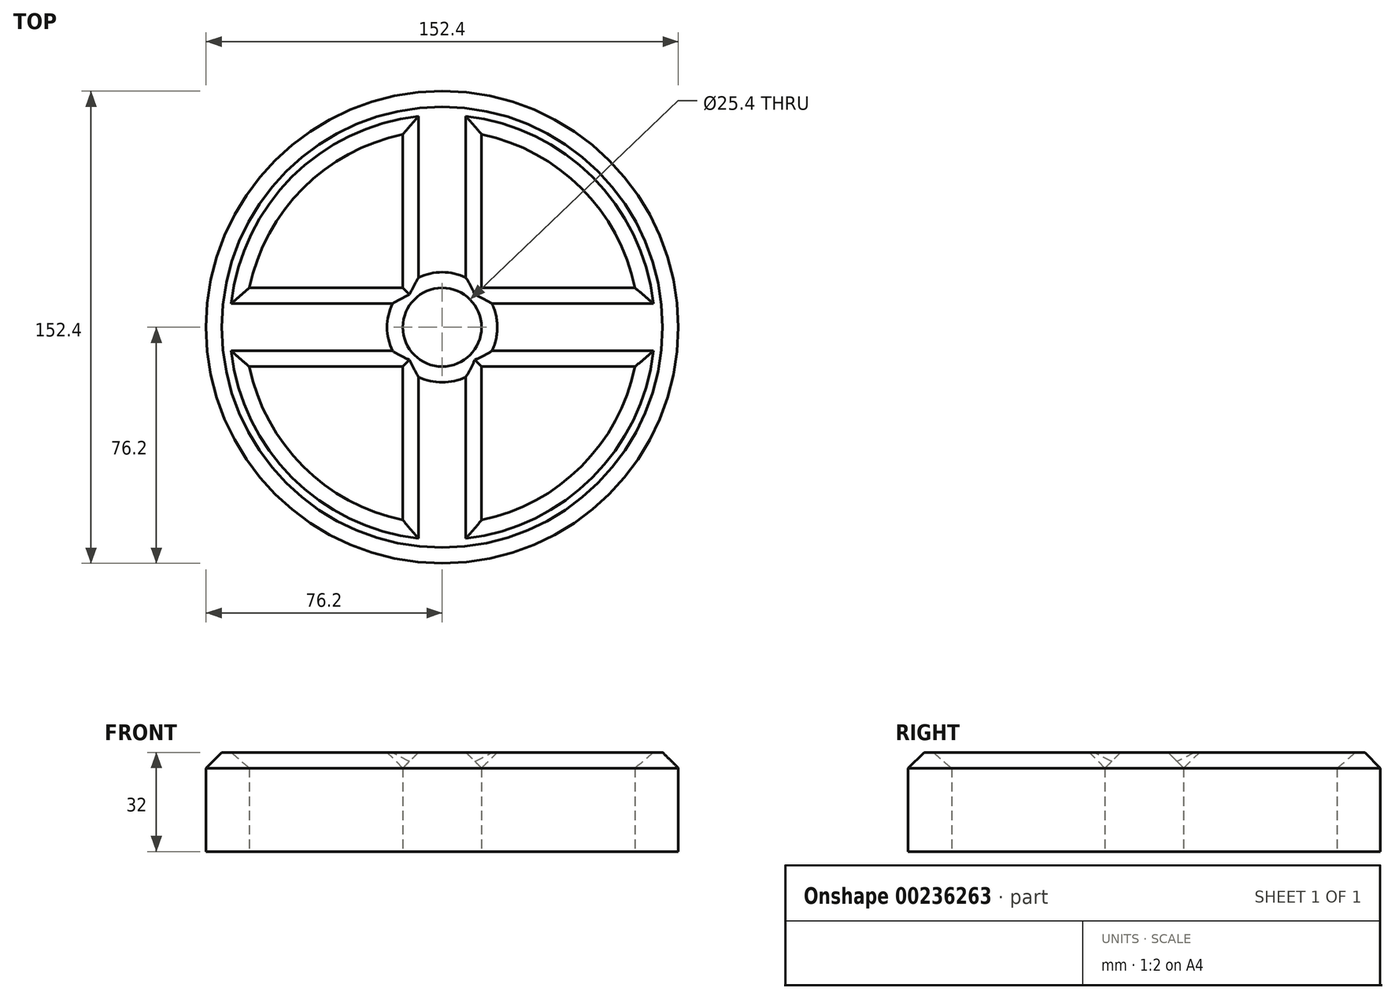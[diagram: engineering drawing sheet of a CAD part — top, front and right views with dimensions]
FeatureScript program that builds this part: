
annotation { "Feature Type Name" : "Feature", "Feature Type Description" : "" }
export const myFeature = defineFeature(function(context is Context, id is Id, definition is map)
    precondition{}
    {
        {
            var Q0;
            Q0=qCreatedBy(makeId("Top.planeOp"),FACE);
            var sketch = newSketch(context, id + "F0", { "sketchPlane" : qUnion([Q0])});
            skCircle(sketch, "E0", {"center": v(0, 0) * mm, "radius": 76.2 * mm});
            skCircle(sketch, "E1", {"center": v(0, 0) * mm, "radius": 12.7 * mm});
            skPoint(sketch, "E2.center.orphan", {"position": v(0, -1.65) * mm});
            skArc(sketch, "E3", {"start": v(-62.22, -12.7) * mm, "mid": v(-44.9, -44.9) * mm, "end": v(-12.7, -62.22) * mm});
            skLineSegment(sketch, "E4", {"start": v(0, 0) * mm, "end": v(0, 63.5) * mm});
            skLineSegment(sketch, "E5.0", {"start": v(12.7, 12.7) * mm, "end": v(12.7, 62.22) * mm});
            skLineSegment(sketch, "E6.0", {"start": v(-12.7, 12.7) * mm, "end": v(-12.7, 62.22) * mm});
            skLineSegment(sketch, "E7", {"start": v(0, -1.65) * mm, "end": v(0, -63.5) * mm});
            skLineSegment(sketch, "E8", {"start": v(0, 0) * mm, "end": v(63.5, 0) * mm});
            skLineSegment(sketch, "E9", {"start": v(0, 0) * mm, "end": v(-76.2, 0) * mm});
            skLineSegment(sketch, "E10.0", {"start": v(-12.7, -12.7) * mm, "end": v(-12.7, -62.22) * mm});
            skLineSegment(sketch, "E11.0", {"start": v(12.7, -12.7) * mm, "end": v(12.7, -62.22) * mm});
            skLineSegment(sketch, "E12.0", {"start": v(12.7, -12.7) * mm, "end": v(62.22, -12.7) * mm});
            skLineSegment(sketch, "E13", {"start": v(-76.2, 0) * mm, "end": v(0, 0) * mm});
            skLineSegment(sketch, "E14.0", {"start": v(-12.7, 12.7) * mm, "end": v(-62.22, 12.7) * mm});
            skLineSegment(sketch, "E15.0", {"start": v(-12.7, -12.7) * mm, "end": v(-62.22, -12.7) * mm});
            skLineSegment(sketch, "E16.0", {"start": v(12.7, 12.7) * mm, "end": v(62.22, 12.7) * mm});
            skLineSegment(sketch, "E17.trimOffspring", {"start": v(-12.7, 75.13) * mm, "end": v(-12.7, 76.2) * mm});
            skLineSegment(sketch, "E18.trimOffspring", {"start": v(12.7, 75.13) * mm, "end": v(12.7, 76.2) * mm});
            skLineSegment(sketch, "E19.trimOffspring", {"start": v(12.7, -75.13) * mm, "end": v(12.7, -76.2) * mm});
            skLineSegment(sketch, "E20.trimOffspring", {"start": v(-12.7, -75.13) * mm, "end": v(-12.7, -76.2) * mm});
            skLineSegment(sketch, "E21.trimOffspring", {"start": v(-75.13, 12.7) * mm, "end": v(-76.2, 12.7) * mm});
            skLineSegment(sketch, "E22.trimOffspring", {"start": v(-75.13, -12.7) * mm, "end": v(-76.2, -12.7) * mm});
            skLineSegment(sketch, "E23.trimOffspring", {"start": v(75.13, -12.7) * mm, "end": v(76.2, -12.7) * mm});
            skLineSegment(sketch, "E24.trimOffspring", {"start": v(75.13, 12.7) * mm, "end": v(76.2, 12.7) * mm});
            skArc(sketch, "E25.trimOffspring", {"start": v(-12.7, 62.22) * mm, "mid": v(-44.9, 44.9) * mm, "end": v(-62.22, 12.7) * mm});
            skArc(sketch, "E26.trimOffspring", {"start": v(62.22, 12.7) * mm, "mid": v(44.9, 44.9) * mm, "end": v(12.7, 62.22) * mm});
            skArc(sketch, "E27.trimOffspring", {"start": v(12.7, -62.22) * mm, "mid": v(44.9, -44.9) * mm, "end": v(62.22, -12.7) * mm});
            skLineSegment(sketch, "E28.bottom", {"start": v(-8.56, -9.38) * mm, "end": v(8.56, -9.38) * mm});
            skLineSegment(sketch, "E28.top", {"start": v(-8.56, 9.38) * mm, "end": v(8.56, 9.38) * mm});
            skLineSegment(sketch, "E28.left", {"start": v(-8.56, -9.38) * mm, "end": v(-8.56, 9.38) * mm});
            skLineSegment(sketch, "E28.right", {"start": v(8.56, -9.38) * mm, "end": v(8.56, 9.38) * mm});
            skLineSegment(sketch, "E29", {"start": v(0, 0) * mm, "end": v(44.9, 44.9) * mm});
            skLineSegment(sketch, "E30", {"start": v(0, 0) * mm, "end": v(-9.18, 8.77) * mm});
            skLineSegment(sketch, "E31", {"start": v(0, 0) * mm, "end": v(44.9, -44.9) * mm});
            skSolve(sketch);
        }
        {
            var Q0;
            Q0 = qSketchRegion(id + "F0", true);
            extrude(context, id + "F1", {"entities" : qUnion([Q0]), "depth" : 32 * mm});
        }
        {
            var Q0;
            Q0 = qSketchRegion(id + "F0", true);
            extrude(context, id + "F2", {"entities" : qUnion([Q0]), "operationType" : NewBodyOperationType.ADD, "depth" : 25.4 * mm});
        }
        {
            var Q0;
            Q0=makeQuery(id+"F1.opExtrude","CAP_FACE",FACE,{"disambiguationData":[OSD([sQuery(id+"F0.wireOp",EDGE,"E0"),sQuery(id+"F0.wireOp",EDGE,"E1"),sQuery(id+"F0.wireOp",EDGE,"E3"),sQuery(id+"F0.wireOp",EDGE,"E5.0"),sQuery(id+"F0.wireOp",EDGE,"E6.0"),sQuery(id+"F0.wireOp",EDGE,"E10.0"),sQuery(id+"F0.wireOp",EDGE,"E11.0"),sQuery(id+"F0.wireOp",EDGE,"E12.0"),sQuery(id+"F0.wireOp",EDGE,"E14.0"),sQuery(id+"F0.wireOp",EDGE,"E15.0"),sQuery(id+"F0.wireOp",EDGE,"E16.0"),sQuery(id+"F0.wireOp",EDGE,"E25.trimOffspring"),sQuery(id+"F0.wireOp",EDGE,"E26.trimOffspring"),sQuery(id+"F0.wireOp",EDGE,"E27.trimOffspring")])],"isStart":false});
            chamfer(context, id + "F3", {"entities" : qUnion([Q0]), "width" : 5.08 * mm, "tangentPropagation" : true});
        }
    });
